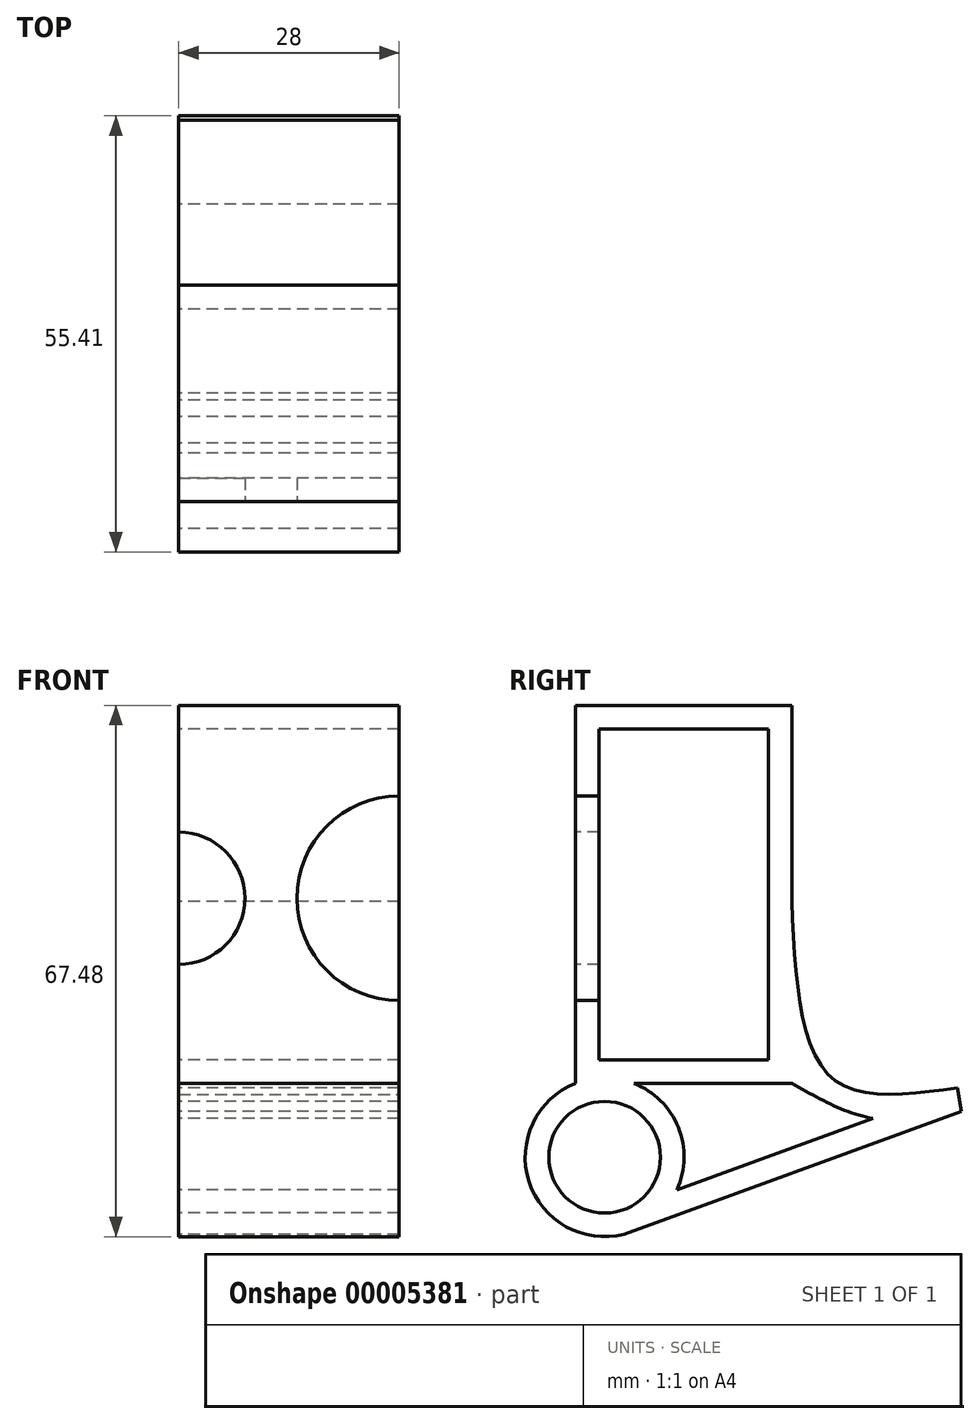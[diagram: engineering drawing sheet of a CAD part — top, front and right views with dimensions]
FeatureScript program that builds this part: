
annotation { "Feature Type Name" : "Feature", "Feature Type Description" : "" }
export const myFeature = defineFeature(function(context is Context, id is Id, definition is map)
    precondition{}
    {
        {
            var Q0;
            Q0=qCreatedBy(makeId("Right.planeOp"),FACE);
            var sketch = newSketch(context, id + "F0", { "sketchPlane" : qUnion([Q0])});
            skLineSegment(sketch, "E0.bottom", {"start": v(-19.41, 23.63) * mm, "end": v(2.09, 23.63) * mm});
            skLineSegment(sketch, "E0.top", {"start": v(-19.41, -18.37) * mm, "end": v(2.09, -18.37) * mm});
            skLineSegment(sketch, "E0.left", {"start": v(-19.41, 23.63) * mm, "end": v(-19.41, -18.37) * mm});
            skLineSegment(sketch, "E0.right", {"start": v(2.09, 23.63) * mm, "end": v(2.09, -18.37) * mm});
            skLineSegment(sketch, "E1.0", {"start": v(-22.41, 26.63) * mm, "end": v(5.09, 26.63) * mm});
            skLineSegment(sketch, "E1.1", {"start": v(-22.41, 26.63) * mm, "end": v(-22.41, -21.37) * mm});
            skLineSegment(sketch, "E1.2", {"start": v(-22.41, -21.37) * mm, "end": v(5.09, -21.37) * mm});
            skLineSegment(sketch, "E1.3", {"start": v(5.09, 26.63) * mm, "end": v(5.09, -21.37) * mm});
            skLineSegment(sketch, "E2", {"start": v(-15.31, -37.01) * mm, "end": v(26.09, -21.94) * mm});
            skLineSegment(sketch, "E3.0", {"start": v(-14.28, -39.83) * mm, "end": v(26.62, -24.94) * mm});
            skLineSegment(sketch, "E4", {"start": v(-15.31, -37.01) * mm, "end": v(-26.5, -41.08) * mm});
            skLineSegment(sketch, "E5", {"start": v(-14.28, -39.83) * mm, "end": v(-34.4, -47.15) * mm});
            skFitSpline(sketch, "E6", {"points": [v(5.09, 1.73) * mm, v(10.15, -20.66) * mm, v(26.09, -21.94) * mm], "startDerivative": vector(2.28, -51.5) * mm, "endDerivative": vector(40.88, 5.87) * mm});
            skFitSpline(sketch, "E7", {"points": [v(5.09, -21.37) * mm, v(15.4, -25.83) * mm, v(26.62, -24.94) * mm], "startDerivative": vector(20.3, -11.77) * mm, "endDerivative": vector(23.73, 4.93) * mm});
            skLineSegment(sketch, "E8", {"start": v(26.09, -21.94) * mm, "end": v(26.62, -24.94) * mm});
            skCircle(sketch, "E9", {"center": v(-18.7, -30.75) * mm, "radius": 10.1 * mm});
            skPoint(sketch, "E9.third.point", {"position": v(-26.5, -37.15) * mm});
            skCircle(sketch, "E10.0", {"center": v(-18.7, -30.75) * mm, "radius": 7.1 * mm});
            skSolve(sketch);
        }
        {
            var Q0;
            {var subQ1=sQuery(id+"F0.wireOp",EDGE,"E4");var subQ5=sQuery(id+"F0.wireOp",EDGE,"E2");var subQ11=makeQuery(id+"F0.imprint","INTERSECT",VERTEX,{"derivedFrom":[subQ5,subQ1]});Q0=makeQuery(id+"F0.imprint","IMPRINT",FACE,{"disambiguationData":[TD([[makeQuery(id+"F0.imprint","IMPRINT",EDGE,{"disambiguationData":[TD([[subQ11,-1.0]])],"derivedFrom":subQ5}),1.0]])]});}
            var Q1;
            Q1=makeQuery(id+"F0.imprint","IMPRINT",FACE,{"disambiguationData":[TD([[makeQuery(id+"F0.imprint","IMPRINT",EDGE,{"derivedFrom":sQuery(id+"F0.wireOp",EDGE,"E0.bottom")}),1.0]])]});
            var Q2;
            {var subQ0=sQuery(id+"F0.wireOp",EDGE,"E6");Q2=makeQuery(id+"F0.imprint","IMPRINT",FACE,{"disambiguationData":[TD([[makeQuery(id+"F0.imprint","IMPRINT",EDGE,{"derivedFrom":subQ0}),-1.0]])]});}
            var Q3;
            {var subQ3=sQuery(id+"F0.wireOp",EDGE,"E3.0");Q3=makeQuery(id+"F0.imprint","IMPRINT",FACE,{"disambiguationData":[TD([[makeQuery(id+"F0.imprint","IMPRINT",EDGE,{"derivedFrom":subQ3}),1.0]])]});}
            var Q4;
            {var subQ0=sQuery(id+"F0.wireOp",EDGE,"E8");Q4=makeQuery(id+"F0.imprint","IMPRINT",FACE,{"disambiguationData":[TD([[makeQuery(id+"F0.imprint","IMPRINT",EDGE,{"derivedFrom":subQ0}),-1.0]])]});}
            var Q5;
            {var subQ1=sQuery(id+"F0.wireOp",EDGE,"E4");var subQ5=sQuery(id+"F0.wireOp",EDGE,"E2");var subQ11=makeQuery(id+"F0.imprint","INTERSECT",VERTEX,{"derivedFrom":[subQ5,subQ1]});Q5=makeQuery(id+"F0.imprint","IMPRINT",FACE,{"disambiguationData":[TD([[makeQuery(id+"F0.imprint","IMPRINT",EDGE,{"disambiguationData":[TD([[subQ11,-1.0]])],"derivedFrom":subQ5}),-1.0]])]});}
            var Q6;
            {var subQ0=sQuery(id+"F0.wireOp",EDGE,"E9");var subQ1=sQuery(id+"F0.wireOp",EDGE,"E1.2");var subQ2=makeQuery(id+"F0.imprint","INTERSECT",VERTEX,{"derivedFrom":[subQ1,subQ0]});Q6=makeQuery(id+"F0.imprint","IMPRINT",FACE,{"disambiguationData":[TD([[makeQuery(id+"F0.imprint","IMPRINT",EDGE,{"disambiguationData":[TD([[subQ2,1.0]])],"derivedFrom":subQ1}),1.0]])]});}
            extrude(context, id + "F1", {"entities" : qUnion([Q0, Q1, Q2, Q3, Q4, Q5, Q6]), "depth" : 28 * mm});
        }
        {
            var Q0;
            Q0=makeQuery(id+"F1.opExtrude","SWEPT_FACE",FACE,{"disambiguationData":[OSD([sQuery(id+"F0.wireOp",EDGE,"E1.1")])]});
            var sketch = newSketch(context, id + "F2", { "sketchPlane" : qUnion([Q0])});
            skLineSegment(sketch, "E11", {"start": v(0, 23.63) * mm, "end": v(28, 23.63) * mm});
            skCircle(sketch, "E12", {"center": v(28, 2.13) * mm, "radius": 13 * mm});
            skCircle(sketch, "E13", {"center": v(0, 2.13) * mm, "radius": 8.4 * mm});
            skSolve(sketch);
        }
        {
            var Q0;
            Q0 = qSketchRegion(id + "F2", true);
            extrude(context, id + "F3", {"entities" : qUnion([Q0]), "operationType" : NewBodyOperationType.REMOVE, "oppositeDirection" : true, "depth" : 3 * mm});
        }
    });
